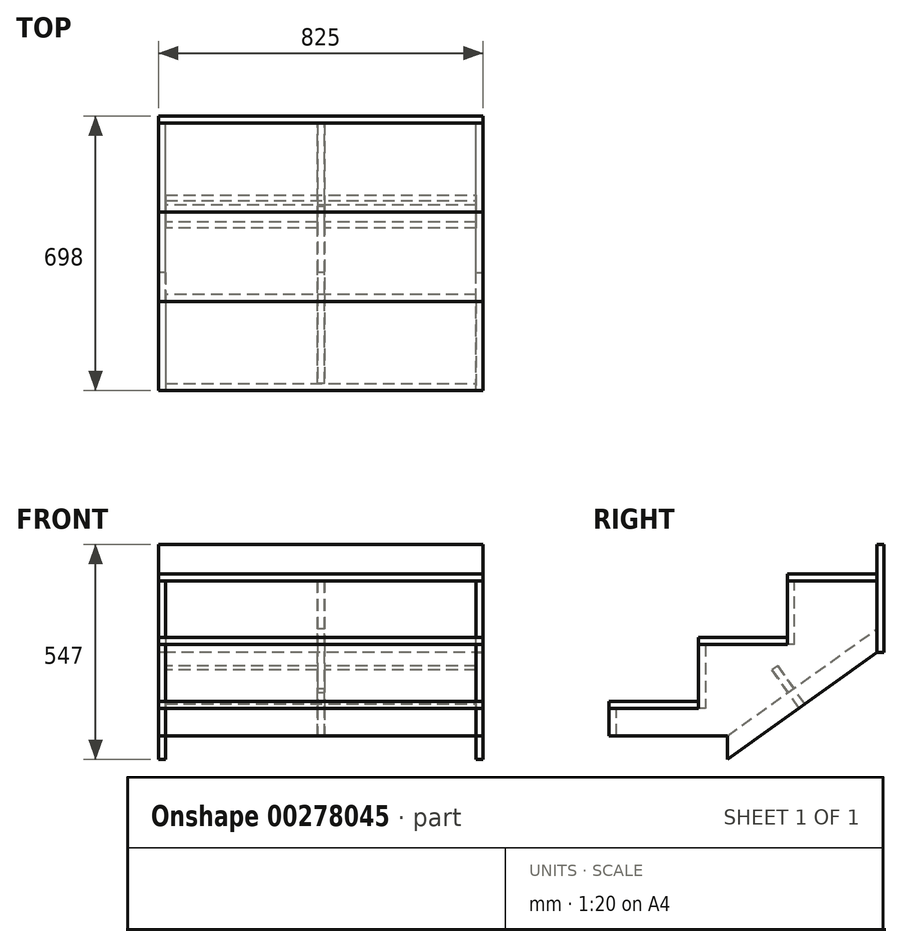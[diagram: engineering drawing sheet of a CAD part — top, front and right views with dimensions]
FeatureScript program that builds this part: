
annotation { "Feature Type Name" : "Feature", "Feature Type Description" : "" }
export const myFeature = defineFeature(function(context is Context, id is Id, definition is map)
    precondition{}
    {
        {
            var Q0;
            Q0=qCreatedBy(makeId("Right.planeOp"),FACE);
            var sketch = newSketch(context, id + "F0", { "sketchPlane" : qUnion([Q0])});
            skLineSegment(sketch, "E0.bottom", {"start": v(0, 0) * mm, "end": v(680, 0) * mm, "construction": true});
            skLineSegment(sketch, "E0.top", {"start": v(0, 632) * mm, "end": v(680, 632) * mm, "construction": true});
            skLineSegment(sketch, "E0.left", {"start": v(0, 0) * mm, "end": v(0, 632) * mm, "construction": true});
            skLineSegment(sketch, "E0.right", {"start": v(680, 0) * mm, "end": v(680, 472) * mm, "construction": true});
            skLineSegment(sketch, "E1.bottom", {"start": v(0, 0) * mm, "end": v(226.67, 0) * mm, "construction": true});
            skLineSegment(sketch, "E1.top", {"start": v(0, 148) * mm, "end": v(226.67, 148) * mm, "construction": true});
            skLineSegment(sketch, "E1.left", {"start": v(0, 0) * mm, "end": v(0, 148) * mm, "construction": true});
            skLineSegment(sketch, "E1.right", {"start": v(226.67, 0) * mm, "end": v(226.67, 148) * mm, "construction": true});
            skLineSegment(sketch, "E2.bottom", {"start": v(226.67, 148) * mm, "end": v(453.33, 148) * mm, "construction": true});
            skLineSegment(sketch, "E2.top", {"start": v(226.67, 310) * mm, "end": v(453.33, 310) * mm, "construction": true});
            skLineSegment(sketch, "E2.left", {"start": v(226.67, 148) * mm, "end": v(226.67, 310) * mm, "construction": true});
            skLineSegment(sketch, "E2.right", {"start": v(453.33, 148) * mm, "end": v(453.33, 310) * mm, "construction": true});
            skLineSegment(sketch, "E3.bottom", {"start": v(453.33, 310) * mm, "end": v(680, 310) * mm, "construction": true});
            skLineSegment(sketch, "E3.top", {"start": v(453.33, 472) * mm, "end": v(680, 472) * mm, "construction": true});
            skLineSegment(sketch, "E3.left", {"start": v(453.33, 310) * mm, "end": v(453.33, 472) * mm, "construction": true});
            skLineSegment(sketch, "E3.right", {"start": v(680, 310) * mm, "end": v(680, 472) * mm, "construction": true});
            skPoint(sketch, "E4", {"position": v(680, 472) * mm});
            skLineSegment(sketch, "E5", {"start": v(680, 472) * mm, "end": v(680, 632) * mm, "construction": true});
            skLineSegment(sketch, "E6.bottom", {"start": v(0, 148) * mm, "end": v(226.67, 148) * mm});
            skLineSegment(sketch, "E6.top", {"start": v(0, 130) * mm, "end": v(226.67, 130) * mm});
            skLineSegment(sketch, "E6.left", {"start": v(0, 148) * mm, "end": v(0, 130) * mm});
            skLineSegment(sketch, "E6.right", {"start": v(226.67, 148) * mm, "end": v(226.67, 130) * mm});
            skLineSegment(sketch, "E7.bottom", {"start": v(226.67, 310) * mm, "end": v(453.33, 310) * mm});
            skLineSegment(sketch, "E7.top", {"start": v(226.67, 292) * mm, "end": v(453.33, 292) * mm});
            skLineSegment(sketch, "E7.left", {"start": v(226.67, 310) * mm, "end": v(226.67, 292) * mm});
            skLineSegment(sketch, "E7.right", {"start": v(453.33, 310) * mm, "end": v(453.33, 292) * mm});
            skLineSegment(sketch, "E8.bottom", {"start": v(453.33, 472) * mm, "end": v(680, 472) * mm});
            skLineSegment(sketch, "E8.top", {"start": v(453.33, 454) * mm, "end": v(680, 454) * mm});
            skLineSegment(sketch, "E8.left", {"start": v(453.33, 472) * mm, "end": v(453.33, 454) * mm});
            skLineSegment(sketch, "E8.right", {"start": v(680, 472) * mm, "end": v(680, 454) * mm});
            skLineSegment(sketch, "E9.bottom", {"start": v(680, 632) * mm, "end": v(980, 632) * mm, "construction": true});
            skLineSegment(sketch, "E9.top", {"start": v(680, 648) * mm, "end": v(980, 648) * mm, "construction": true});
            skLineSegment(sketch, "E9.left", {"start": v(680, 632) * mm, "end": v(680, 648) * mm, "construction": true});
            skLineSegment(sketch, "E10", {"start": v(0, 162) * mm, "end": v(226.67, 162) * mm, "construction": true});
            skLineSegment(sketch, "E11", {"start": v(453.33, 324) * mm, "end": v(226.67, 324) * mm, "construction": true});
            skLineSegment(sketch, "E12", {"start": v(226.67, 310) * mm, "end": v(226.67, 324) * mm, "construction": true});
            skLineSegment(sketch, "E13", {"start": v(453.33, 472) * mm, "end": v(453.33, 486) * mm, "construction": true});
            skLineSegment(sketch, "E14", {"start": v(453.33, 486) * mm, "end": v(680, 486) * mm, "construction": true});
            skLineSegment(sketch, "E15", {"start": v(0, 148) * mm, "end": v(0, 162) * mm, "construction": true});
            skLineSegment(sketch, "E16", {"start": v(113.33, 162) * mm, "end": v(113.33, 0) * mm, "construction": true});
            skLineSegment(sketch, "E17", {"start": v(830, 648) * mm, "end": v(830, 486) * mm, "construction": true});
            skLineSegment(sketch, "E18", {"start": v(680, 486) * mm, "end": v(980, 486) * mm, "construction": true});
            skLineSegment(sketch, "E19", {"start": v(980, 648) * mm, "end": v(980, 486) * mm, "construction": true});
            skLineSegment(sketch, "E20", {"start": v(453.33, 324) * mm, "end": v(680, 324) * mm, "construction": true});
            skLineSegment(sketch, "E21", {"start": v(566.67, 324) * mm, "end": v(566.67, 486) * mm, "construction": true});
            skLineSegment(sketch, "E22", {"start": v(226.67, 162) * mm, "end": v(453.33, 162) * mm, "construction": true});
            skLineSegment(sketch, "E23", {"start": v(340, 162) * mm, "end": v(340, 324) * mm, "construction": true});
            skSolve(sketch);
        }
        {
            var Q0;
            Q0=makeQuery(id+"F0.imprint","IMPRINT",FACE,{"disambiguationData":[TD([[makeQuery(id+"F0.imprint","IMPRINT",EDGE,{"derivedFrom":sQuery(id+"F0.wireOp",EDGE,"E7.bottom")}),-1.0]])]});
            var Q1;
            Q1=makeQuery(id+"F0.imprint","IMPRINT",FACE,{"disambiguationData":[TD([[makeQuery(id+"F0.imprint","IMPRINT",EDGE,{"derivedFrom":sQuery(id+"F0.wireOp",EDGE,"E8.bottom")}),-1.0]])]});
            var Q2;
            Q2=makeQuery(id+"F0.imprint","IMPRINT",FACE,{"disambiguationData":[TD([[makeQuery(id+"F0.imprint","IMPRINT",EDGE,{"derivedFrom":sQuery(id+"F0.wireOp",EDGE,"E6.bottom")}),-1.0]])]});
            extrude(context, id + "F1", {"entities" : qUnion([Q0, Q1, Q2]), "depth" : 825 * mm, "offsetDistance" : 25 * mm});
        }
        {
            var Q0;
            Q0=qCreatedBy(makeId("Right.planeOp"),FACE);
            var sketch = newSketch(context, id + "F2", { "sketchPlane" : qUnion([Q0])});
            skLineSegment(sketch, "E24.bottom", {"start": v(0, 0) * mm, "end": v(300, 0) * mm});
            skLineSegment(sketch, "E24.top", {"start": v(0, 60) * mm, "end": v(300, 60) * mm});
            skLineSegment(sketch, "E24.left", {"start": v(0, 0) * mm, "end": v(0, 60) * mm});
            skLineSegment(sketch, "E24.right", {"start": v(300, 0) * mm, "end": v(300, 60) * mm});
            skSolve(sketch);
        }
        {
            var Q0;
            Q0=qCreatedBy(makeId("Right.planeOp"),FACE);
            var sketch = newSketch(context, id + "F3", { "sketchPlane" : qUnion([Q0])});
            skLineSegment(sketch, "E25.0", {"start": v(0, 0) * mm, "end": v(680, 0) * mm, "construction": true});
            skLineSegment(sketch, "E25.1", {"start": v(0, 632) * mm, "end": v(680, 632) * mm, "construction": true});
            skLineSegment(sketch, "E25.2", {"start": v(0, 0) * mm, "end": v(0, 632) * mm, "construction": true});
            skLineSegment(sketch, "E25.3", {"start": v(680, 0) * mm, "end": v(680, 472) * mm, "construction": true});
            skLineSegment(sketch, "E25.4", {"start": v(0, 0) * mm, "end": v(226.67, 0) * mm, "construction": true});
            skLineSegment(sketch, "E25.5", {"start": v(0, 148) * mm, "end": v(226.67, 148) * mm, "construction": true});
            skLineSegment(sketch, "E25.6", {"start": v(0, 0) * mm, "end": v(0, 148) * mm, "construction": true});
            skLineSegment(sketch, "E25.7", {"start": v(226.67, 0) * mm, "end": v(226.67, 148) * mm, "construction": true});
            skLineSegment(sketch, "E25.8", {"start": v(226.67, 148) * mm, "end": v(453.33, 148) * mm, "construction": true});
            skLineSegment(sketch, "E25.9", {"start": v(226.67, 310) * mm, "end": v(453.33, 310) * mm, "construction": true});
            skLineSegment(sketch, "E25.10", {"start": v(226.67, 148) * mm, "end": v(226.67, 310) * mm, "construction": true});
            skLineSegment(sketch, "E25.11", {"start": v(453.33, 148) * mm, "end": v(453.33, 310) * mm, "construction": true});
            skLineSegment(sketch, "E25.12", {"start": v(453.33, 310) * mm, "end": v(680, 310) * mm, "construction": true});
            skLineSegment(sketch, "E25.13", {"start": v(453.33, 472) * mm, "end": v(680, 472) * mm, "construction": true});
            skLineSegment(sketch, "E25.14", {"start": v(453.33, 310) * mm, "end": v(453.33, 472) * mm, "construction": true});
            skLineSegment(sketch, "E25.15", {"start": v(680, 310) * mm, "end": v(680, 472) * mm, "construction": true});
            skPoint(sketch, "E25.16", {"position": v(680, 472) * mm});
            skLineSegment(sketch, "E25.17", {"start": v(680, 472) * mm, "end": v(680, 632) * mm, "construction": true});
            skLineSegment(sketch, "E25.18", {"start": v(0, 148) * mm, "end": v(226.67, 148) * mm, "construction": true});
            skLineSegment(sketch, "E25.19", {"start": v(0, 130) * mm, "end": v(226.67, 130) * mm, "construction": true});
            skLineSegment(sketch, "E25.20", {"start": v(0, 148) * mm, "end": v(0, 130) * mm, "construction": true});
            skLineSegment(sketch, "E25.21", {"start": v(226.67, 148) * mm, "end": v(226.67, 130) * mm, "construction": true});
            skLineSegment(sketch, "E25.22", {"start": v(226.67, 310) * mm, "end": v(453.33, 310) * mm, "construction": true});
            skLineSegment(sketch, "E25.23", {"start": v(226.67, 292) * mm, "end": v(453.33, 292) * mm, "construction": true});
            skLineSegment(sketch, "E25.24", {"start": v(226.67, 310) * mm, "end": v(226.67, 292) * mm, "construction": true});
            skLineSegment(sketch, "E25.25", {"start": v(453.33, 310) * mm, "end": v(453.33, 292) * mm, "construction": true});
            skLineSegment(sketch, "E25.26", {"start": v(453.33, 472) * mm, "end": v(680, 472) * mm, "construction": true});
            skLineSegment(sketch, "E25.27", {"start": v(453.33, 454) * mm, "end": v(680, 454) * mm, "construction": true});
            skLineSegment(sketch, "E25.28", {"start": v(453.33, 472) * mm, "end": v(453.33, 454) * mm, "construction": true});
            skLineSegment(sketch, "E25.29", {"start": v(680, 472) * mm, "end": v(680, 454) * mm, "construction": true});
            skLineSegment(sketch, "E26", {"start": v(0, 130) * mm, "end": v(453.33, 454) * mm, "construction": true});
            skLineSegment(sketch, "E27", {"start": v(300, 0) * mm, "end": v(680, 271.59) * mm});
            skLineSegment(sketch, "E28", {"start": v(453.33, 454) * mm, "end": v(680, 454) * mm});
            skLineSegment(sketch, "E29", {"start": v(680, 454) * mm, "end": v(680, 271.59) * mm});
            skLineSegment(sketch, "E30", {"start": v(453.33, 454) * mm, "end": v(453.33, 292) * mm});
            skLineSegment(sketch, "E31", {"start": v(226.67, 292) * mm, "end": v(453.33, 292) * mm});
            skLineSegment(sketch, "E32", {"start": v(226.67, 292) * mm, "end": v(226.67, 130) * mm});
            skLineSegment(sketch, "E33", {"start": v(226.67, 130) * mm, "end": v(0, 130) * mm});
            skLineSegment(sketch, "E34", {"start": v(0, 130) * mm, "end": v(0, 0) * mm});
            skLineSegment(sketch, "E35", {"start": v(0, 0) * mm, "end": v(300, 0) * mm});
            skLineSegment(sketch, "E36", {"start": v(453.33, 454) * mm, "end": v(680, 616) * mm, "construction": true});
            skLineSegment(sketch, "E37", {"start": v(680, 616) * mm, "end": v(842.93, 388.03) * mm, "construction": true});
            skLineSegment(sketch, "E38", {"start": v(842.93, 388.03) * mm, "end": v(680, 271.59) * mm, "construction": true});
            skLineSegment(sketch, "E39", {"start": v(0, 130) * mm, "end": v(-162.93, 13.55) * mm, "construction": true});
            skLineSegment(sketch, "E40", {"start": v(-162.93, 13.55) * mm, "end": v(0, -214.41) * mm, "construction": true});
            skLineSegment(sketch, "E41", {"start": v(0, -214.41) * mm, "end": v(300, 0) * mm, "construction": true});
            skLineSegment(sketch, "E42", {"start": v(0, 0) * mm, "end": v(0, -214.41) * mm, "construction": true});
            skSolve(sketch);
        }
        {
            var Q0;
            Q0=makeQuery(id+"F3.imprint","IMPRINT",FACE,{"disambiguationData":[TD([[makeQuery(id+"F3.imprint","IMPRINT",EDGE,{"derivedFrom":sQuery(id+"F3.wireOp",EDGE,"E27")}),1.0]])]});
            extrude(context, id + "F4", {"entities" : qUnion([Q0]), "depth" : 18 * mm, "offsetDistance" : 25 * mm});
        }
        {
            var Q0;
            Q0=makeQuery(id+"F1.opExtrude","SWEPT_EDGE",EDGE,{"disambiguationData":[OSD([sQuery(id+"F0.wireOp",EDGE,"E7.bottom"),sQuery(id+"F0.wireOp",EDGE,"E7.left")])]});
            cPoint(context, id + "F5", {"entities" : qUnion([Q0]), "parameter" : 0.5});
        }
        {
            var Q0;
            Q0=qCreatedBy(makeId("Right.planeOp"),FACE);
            var Q1;
            Q1 = qCreatedBy(id + "F5" ,VERTEX);
            cPlane(context, id + "F6", {"entities" : qUnion([Q0, Q1]), "cplaneType" : CPlaneType.PLANE_POINT, "offset" : 25 * mm, "width" : 150 * mm, "height" : 150 * mm});
        }
        {
            var Q0;
            Q0=makeQuery(id+"F4.opExtrude","SWEPT_BODY",BODY,{"disambiguationData":[OSD([sQuery(id+"F3.wireOp",EDGE,"E27"),sQuery(id+"F3.wireOp",EDGE,"E28"),sQuery(id+"F3.wireOp",EDGE,"E29"),sQuery(id+"F3.wireOp",EDGE,"E30"),sQuery(id+"F3.wireOp",EDGE,"E31"),sQuery(id+"F3.wireOp",EDGE,"E32"),sQuery(id+"F3.wireOp",EDGE,"E33"),sQuery(id+"F3.wireOp",EDGE,"E34"),sQuery(id+"F3.wireOp",EDGE,"E35")])]});
            var Q1;
            Q1=qCreatedBy(id+"F6.planeOp",FACE);
            mirror(context, id + "F7", {"entities" : qUnion([Q0]), "mirrorPlane" : qUnion([Q1])});
        }
        {
            var Q0;
            Q0=makeQuery(id+"F4.opExtrude","CAP_FACE",FACE,{"disambiguationData":[OSD([sQuery(id+"F3.wireOp",EDGE,"E27"),sQuery(id+"F3.wireOp",EDGE,"E28"),sQuery(id+"F3.wireOp",EDGE,"E29"),sQuery(id+"F3.wireOp",EDGE,"E30"),sQuery(id+"F3.wireOp",EDGE,"E31"),sQuery(id+"F3.wireOp",EDGE,"E32"),sQuery(id+"F3.wireOp",EDGE,"E33"),sQuery(id+"F3.wireOp",EDGE,"E34"),sQuery(id+"F3.wireOp",EDGE,"E35")])],"isStart":false});
            var sketch = newSketch(context, id + "F8", { "sketchPlane" : qUnion([Q0])});
            skLineSegment(sketch, "E43.bottom", {"start": v(0, 130) * mm, "end": v(18, 130) * mm});
            skLineSegment(sketch, "E43.top", {"start": v(0, 0) * mm, "end": v(18, 0) * mm});
            skLineSegment(sketch, "E43.left", {"start": v(0, 130) * mm, "end": v(0, 0) * mm});
            skLineSegment(sketch, "E43.right", {"start": v(18, 130) * mm, "end": v(18, 0) * mm});
            skLineSegment(sketch, "E44.bottom", {"start": v(226.67, 292) * mm, "end": v(244.67, 292) * mm});
            skLineSegment(sketch, "E44.top", {"start": v(226.67, 130) * mm, "end": v(244.67, 130) * mm});
            skLineSegment(sketch, "E44.left", {"start": v(226.67, 292) * mm, "end": v(226.67, 130) * mm});
            skLineSegment(sketch, "E44.right", {"start": v(244.67, 292) * mm, "end": v(244.67, 130) * mm});
            skLineSegment(sketch, "E45.bottom", {"start": v(453.33, 454) * mm, "end": v(471.33, 454) * mm});
            skLineSegment(sketch, "E45.top", {"start": v(453.33, 292) * mm, "end": v(471.33, 292) * mm});
            skLineSegment(sketch, "E45.left", {"start": v(453.33, 454) * mm, "end": v(453.33, 292) * mm});
            skLineSegment(sketch, "E45.right", {"start": v(471.33, 454) * mm, "end": v(471.33, 292) * mm});
            skSolve(sketch);
        }
        {
            var Q0;
            Q0 = qSketchRegion(id + "F8", true);
            var Q1;
            Q1=makeQuery(id+"F7.opPattern","COPY",BODY,{"derivedFrom":makeQuery(id+"F4.opExtrude","SWEPT_BODY",BODY,{"disambiguationData":[OSD([sQuery(id+"F3.wireOp",EDGE,"E27"),sQuery(id+"F3.wireOp",EDGE,"E28"),sQuery(id+"F3.wireOp",EDGE,"E29"),sQuery(id+"F3.wireOp",EDGE,"E30"),sQuery(id+"F3.wireOp",EDGE,"E31"),sQuery(id+"F3.wireOp",EDGE,"E32"),sQuery(id+"F3.wireOp",EDGE,"E33"),sQuery(id+"F3.wireOp",EDGE,"E34"),sQuery(id+"F3.wireOp",EDGE,"E35")])]}),"instanceName":"1"});
            extrude(context, id + "F9", {"entities" : qUnion([Q0]), "endBound" : BoundingType.UP_TO_BODY, "depth" : 25 * mm, "endBoundEntityBody" : qUnion([Q1]), "offsetDistance" : 25 * mm});
        }
        {
            var Q0;
            Q0=makeQuery(id+"F7.opPattern","COPY",FACE,{"derivedFrom":makeQuery(id+"F4.opExtrude","SWEPT_FACE",FACE,{"disambiguationData":[OSD([sQuery(id+"F3.wireOp",EDGE,"E29")])]}),"instanceName":"1"});
            var sketch = newSketch(context, id + "F10", { "sketchPlane" : qUnion([Q0])});
            skLineSegment(sketch, "E46.bottom", {"start": v(-825, 271.59) * mm, "end": v(0, 271.59) * mm});
            skLineSegment(sketch, "E46.top", {"start": v(-825, 547) * mm, "end": v(0, 547) * mm});
            skLineSegment(sketch, "E46.left", {"start": v(-825, 271.59) * mm, "end": v(-825, 547) * mm});
            skLineSegment(sketch, "E46.right", {"start": v(0, 271.59) * mm, "end": v(0, 547) * mm});
            skSolve(sketch);
        }
        {
            var Q0;
            Q0 = qSketchRegion(id + "F10", true);
            extrude(context, id + "F11", {"entities" : qUnion([Q0]), "depth" : 18 * mm, "offsetDistance" : 25 * mm});
        }
        {
            var Q0;
            Q0 = qSketchRegion(id + "F2", true);
            extrude(context, id + "F12", {"entities" : qUnion([Q0]), "operationType" : NewBodyOperationType.REMOVE, "endBound" : BoundingType.THROUGH_ALL, "depth" : 25 * mm, "offsetDistance" : 25 * mm});
        }
        {
            var Q0;
            Q0=qCreatedBy(id+"F6.planeOp",FACE);
            var sketch = newSketch(context, id + "F13", { "sketchPlane" : qUnion([Q0])});
            skLineSegment(sketch, "E47", {"start": v(18, 60) * mm, "end": v(300, 60) * mm});
            skLineSegment(sketch, "E48", {"start": v(300, 60) * mm, "end": v(680, 331.59) * mm});
            skLineSegment(sketch, "E49", {"start": v(680, 331.59) * mm, "end": v(680, 454) * mm});
            skLineSegment(sketch, "E50", {"start": v(680, 454) * mm, "end": v(471.33, 454) * mm});
            skLineSegment(sketch, "E51", {"start": v(471.33, 454) * mm, "end": v(471.33, 292) * mm});
            skLineSegment(sketch, "E52", {"start": v(471.33, 292) * mm, "end": v(244.67, 292) * mm});
            skLineSegment(sketch, "E53", {"start": v(244.67, 292) * mm, "end": v(244.67, 130) * mm});
            skLineSegment(sketch, "E54", {"start": v(244.67, 130) * mm, "end": v(18, 130) * mm});
            skLineSegment(sketch, "E55", {"start": v(18, 130) * mm, "end": v(18, 60) * mm});
            skSolve(sketch);
        }
        {
            var Q0;
            Q0 = qSketchRegion(id + "F13", true);
            extrude(context, id + "F14", {"entities" : qUnion([Q0]), "endBound" : BoundingType.SYMMETRIC, "depth" : 18 * mm, "offsetDistance" : 25 * mm});
        }
        {
            var Q0;
            Q0=qCreatedBy(id+"F6.planeOp",FACE);
            var sketch = newSketch(context, id + "F15", { "sketchPlane" : qUnion([Q0])});
            skLineSegment(sketch, "E56", {"start": v(490, 135.8) * mm, "end": v(355.49, 324) * mm, "construction": true});
            skSolve(sketch);
        }
        {
            var Q0;
            Q0=makeQuery(id+"F14.opExtrude","SWEPT_FACE",FACE,{"disambiguationData":[OSD([sQuery(id+"F13.wireOp",EDGE,"E48")])]});
            var sketch = newSketch(context, id + "F16", { "sketchPlane" : qUnion([Q0])});
            skLineSegment(sketch, "E57.bottom", {"start": v(807, -468.6) * mm, "end": v(18, -468.6) * mm});
            skLineSegment(sketch, "E57.top", {"start": v(807, -486.6) * mm, "end": v(18, -486.6) * mm});
            skLineSegment(sketch, "E57.left", {"start": v(807, -468.6) * mm, "end": v(807, -486.6) * mm});
            skLineSegment(sketch, "E57.right", {"start": v(18, -468.6) * mm, "end": v(18, -486.6) * mm});
            skLineSegment(sketch, "E58", {"start": v(412.5, -468.6) * mm, "end": v(412.5, -486.6) * mm, "construction": true});
            skSolve(sketch);
        }
        {
            var Q0;
            Q0 = qSketchRegion(id + "F16", true);
            var Q1;
            Q1=makeQuery(id+"F7.opPattern","COPY",FACE,{"derivedFrom":makeQuery(id+"F4.opExtrude","SWEPT_FACE",FACE,{"disambiguationData":[OSD([sQuery(id+"F3.wireOp",EDGE,"E27")])]}),"instanceName":"1"});
            extrude(context, id + "F17", {"entities" : qUnion([Q0]), "endBound" : BoundingType.UP_TO_SURFACE, "depth" : 26 * mm, "endBoundEntityFace" : qUnion([Q1]), "offsetDistance" : 25 * mm, "hasSecondDirection" : true, "secondDirectionOppositeDirection" : true, "secondDirectionDepth" : 70 * mm});
        }
        {
            var Q0;
            Q0=makeQuery(id+"F14.opExtrude","SWEPT_BODY",BODY,{"disambiguationData":[OSD([sQuery(id+"F13.wireOp",EDGE,"E47"),sQuery(id+"F13.wireOp",EDGE,"E48"),sQuery(id+"F13.wireOp",EDGE,"E49"),sQuery(id+"F13.wireOp",EDGE,"E50"),sQuery(id+"F13.wireOp",EDGE,"E51"),sQuery(id+"F13.wireOp",EDGE,"E52"),sQuery(id+"F13.wireOp",EDGE,"E53"),sQuery(id+"F13.wireOp",EDGE,"E54"),sQuery(id+"F13.wireOp",EDGE,"E55")])]});
            var Q1;
            Q1=makeQuery(id+"F17.opExtrude","SWEPT_BODY",BODY,{"disambiguationData":[OSD([sQuery(id+"F16.wireOp",EDGE,"E57.bottom"),sQuery(id+"F16.wireOp",EDGE,"E57.top"),sQuery(id+"F16.wireOp",EDGE,"E57.left"),sQuery(id+"F16.wireOp",EDGE,"E57.right")])]});
            booleanBodies(context, id + "F18", {"operationType" : BooleanOperationType.SUBTRACTION, "tools" : qUnion([Q0]), "targets" : qUnion([Q1]), "keepTools" : true});
        }
    });
